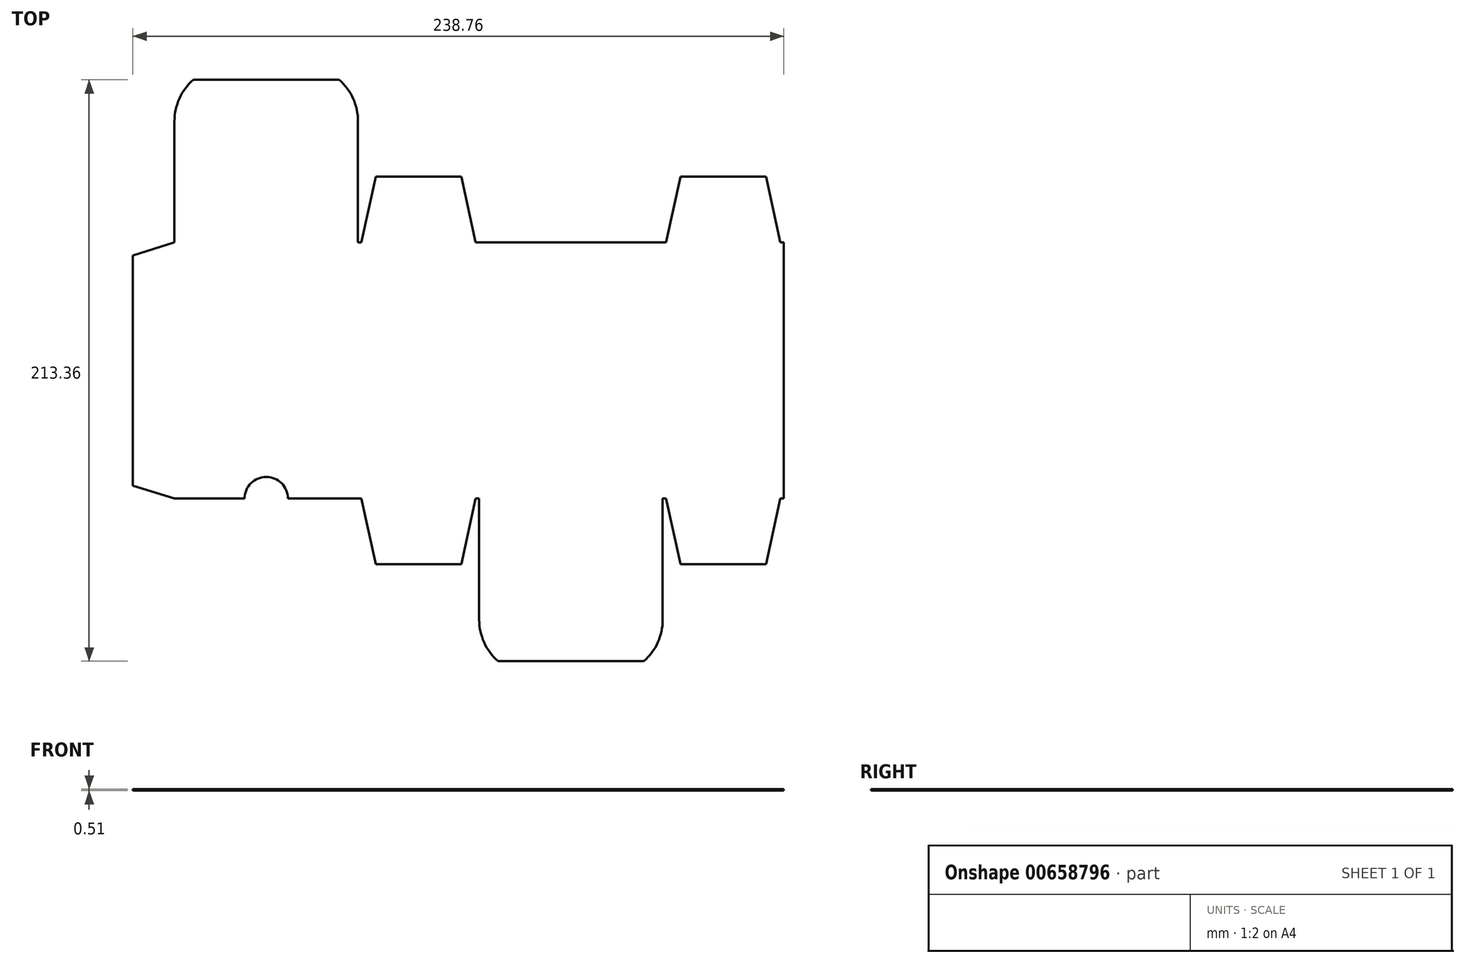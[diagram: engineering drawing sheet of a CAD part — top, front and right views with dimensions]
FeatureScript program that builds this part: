
annotation { "Feature Type Name" : "Feature", "Feature Type Description" : "" }
export const myFeature = defineFeature(function(context is Context, id is Id, definition is map)
    precondition{}
    {
        {
            var Q0;
            Q0=qCreatedBy(makeId("Top.planeOp"),FACE);
            var sketch = newSketch(context, id + "F0", { "sketchPlane" : qUnion([Q0])});
            skLineSegment(sketch, "E0.bottom", {"start": v(0, 0) * mm, "end": v(25.72, 0) * mm});
            skLineSegment(sketch, "E0.top", {"start": v(0, 93.98) * mm, "end": v(67.3, 93.98) * mm, "construction": true});
            skLineSegment(sketch, "E0.left", {"start": v(0, 0) * mm, "end": v(0, 93.98) * mm, "construction": true});
            skLineSegment(sketch, "E0.right", {"start": v(67.31, 0) * mm, "end": v(67.31, 93.98) * mm, "construction": true});
            skLineSegment(sketch, "E1", {"start": v(0, 93.98) * mm, "end": v(0, 138.43) * mm});
            skLineSegment(sketch, "E2", {"start": v(0, 138.43) * mm, "end": v(67.3, 138.43) * mm, "construction": true});
            skLineSegment(sketch, "E3", {"start": v(67.3, 138.43) * mm, "end": v(67.3, 93.98) * mm});
            skLineSegment(sketch, "E4", {"start": v(67.31, 0) * mm, "end": v(68.58, 0) * mm, "construction": true});
            skLineSegment(sketch, "E5", {"start": v(111.76, 93.98) * mm, "end": v(111.76, 0) * mm, "construction": true});
            skLineSegment(sketch, "E6", {"start": v(111.76, 0) * mm, "end": v(179.07, 0) * mm, "construction": true});
            skLineSegment(sketch, "E7", {"start": v(179.07, 0) * mm, "end": v(179.07, 93.98) * mm, "construction": true});
            skLineSegment(sketch, "E8", {"start": v(111.76, 93.98) * mm, "end": v(179.07, 93.98) * mm});
            skArc(sketch, "E9", {"start": v(6.88, 153.67) * mm, "mid": v(1.8, 146.8) * mm, "end": v(0, 138.43) * mm});
            skLineSegment(sketch, "E10", {"start": v(33.65, 93.98) * mm, "end": v(33.65, 138.43) * mm, "construction": true});
            skLineSegment(sketch, "E11", {"start": v(6.88, 153.67) * mm, "end": v(33.65, 153.67) * mm});
            skLineSegment(sketch, "E12.MirrorCS", {"start": v(60.43, 153.67) * mm, "end": v(33.65, 153.67) * mm});
            skArc(sketch, "E13.MirrorCS", {"start": v(60.43, 153.67) * mm, "mid": v(65.51, 146.8) * mm, "end": v(67.3, 138.43) * mm});
            skLineSegment(sketch, "E14", {"start": v(0, 47) * mm, "end": v(67.31, 47) * mm, "construction": true});
            skLineSegment(sketch, "E15", {"start": v(0, 93.98) * mm, "end": v(-15.24, 89.22) * mm});
            skLineSegment(sketch, "E16", {"start": v(-15.24, 89.22) * mm, "end": v(-15.24, 46.99) * mm});
            skLineSegment(sketch, "E17.MirrorCS", {"start": v(0, 0) * mm, "end": v(-15.24, 4.76) * mm});
            skLineSegment(sketch, "E18.MirrorCS", {"start": v(-15.24, 4.76) * mm, "end": v(-15.24, 46.99) * mm});
            skArc(sketch, "E19", {"start": v(41.6, 0) * mm, "mid": v(33.66, 7.94) * mm, "end": v(25.72, 0) * mm});
            skLineSegment(sketch, "E20.trimOffspring", {"start": v(41.6, 0) * mm, "end": v(67.31, 0) * mm});
            skLineSegment(sketch, "E21", {"start": v(67.3, 93.98) * mm, "end": v(68.58, 93.98) * mm});
            skLineSegment(sketch, "E22", {"start": v(111.76, 93.98) * mm, "end": v(110.5, 93.98) * mm});
            skLineSegment(sketch, "E23", {"start": v(89.53, 93.98) * mm, "end": v(89.53, 118.11) * mm, "construction": true});
            skLineSegment(sketch, "E24", {"start": v(68.58, 93.98) * mm, "end": v(73.86, 118.11) * mm});
            skLineSegment(sketch, "E25.MirrorCS", {"start": v(110.5, 93.98) * mm, "end": v(105.21, 118.11) * mm});
            skLineSegment(sketch, "E26", {"start": v(73.86, 118.11) * mm, "end": v(105.21, 118.11) * mm});
            skLineSegment(sketch, "E27.MirrorCS", {"start": v(110.5, 0) * mm, "end": v(105.21, -24.13) * mm});
            skLineSegment(sketch, "E28.MirrorCS", {"start": v(68.58, 0) * mm, "end": v(73.86, -24.13) * mm});
            skLineSegment(sketch, "E29.MirrorCS", {"start": v(73.86, -24.13) * mm, "end": v(105.21, -24.13) * mm});
            skLineSegment(sketch, "E30", {"start": v(179.07, 93.98) * mm, "end": v(223.52, 93.98) * mm, "construction": true});
            skLineSegment(sketch, "E31", {"start": v(223.52, 0) * mm, "end": v(223.52, 93.98) * mm});
            skLineSegment(sketch, "E32", {"start": v(145.42, 93.98) * mm, "end": v(145.42, 0) * mm, "construction": true});
            skLineSegment(sketch, "E33.MirrorCS", {"start": v(180.34, 93.98) * mm, "end": v(185.62, 118.11) * mm});
            skLineSegment(sketch, "E34.MirrorCS", {"start": v(216.97, 118.11) * mm, "end": v(185.62, 118.11) * mm});
            skLineSegment(sketch, "E35.MirrorCS", {"start": v(222.25, 93.98) * mm, "end": v(216.97, 118.11) * mm});
            skLineSegment(sketch, "E36.MirrorCS", {"start": v(222.25, 0) * mm, "end": v(216.97, -24.13) * mm});
            skLineSegment(sketch, "E37.MirrorCS", {"start": v(216.97, -24.13) * mm, "end": v(185.62, -24.13) * mm});
            skLineSegment(sketch, "E38.MirrorCS", {"start": v(180.34, 0) * mm, "end": v(185.62, -24.13) * mm});
            skLineSegment(sketch, "E39", {"start": v(68.58, 93.98) * mm, "end": v(110.5, 93.98) * mm, "construction": true});
            skLineSegment(sketch, "E40.trimOffspring", {"start": v(110.5, 0) * mm, "end": v(111.76, 0) * mm, "construction": true});
            skLineSegment(sketch, "E41", {"start": v(67.31, 0) * mm, "end": v(68.58, 0) * mm});
            skLineSegment(sketch, "E42", {"start": v(111.76, 0) * mm, "end": v(110.5, 0) * mm});
            skLineSegment(sketch, "E43", {"start": v(68.58, 0) * mm, "end": v(110.5, 0) * mm, "construction": true});
            skLineSegment(sketch, "E44", {"start": v(179.07, 0) * mm, "end": v(180.34, 0) * mm});
            skLineSegment(sketch, "E45.trimOffspring", {"start": v(222.25, 0) * mm, "end": v(223.52, 0) * mm});
            skLineSegment(sketch, "E46", {"start": v(180.34, 0) * mm, "end": v(222.25, 0) * mm, "construction": true});
            skLineSegment(sketch, "E47", {"start": v(111.76, 0) * mm, "end": v(111.76, -44.45) * mm});
            skLineSegment(sketch, "E48", {"start": v(179.07, 0) * mm, "end": v(179.07, -44.45) * mm});
            skLineSegment(sketch, "E49", {"start": v(111.76, -44.45) * mm, "end": v(179.07, -44.45) * mm, "construction": true});
            skArc(sketch, "E50", {"start": v(172.2, -59.69) * mm, "mid": v(177.27, -52.81) * mm, "end": v(179.07, -44.45) * mm});
            skArc(sketch, "E51", {"start": v(111.76, -44.45) * mm, "mid": v(113.56, -52.81) * mm, "end": v(118.64, -59.7) * mm});
            skLineSegment(sketch, "E52", {"start": v(172.2, -59.7) * mm, "end": v(118.64, -59.7) * mm});
            skLineSegment(sketch, "E53", {"start": v(179.07, 93.98) * mm, "end": v(180.34, 93.98) * mm});
            skLineSegment(sketch, "E54", {"start": v(222.25, 93.98) * mm, "end": v(223.52, 93.98) * mm});
            skSolve(sketch);
        }
        {
            var Q0;
            Q0=makeQuery(id+"F0.imprint","IMPRINT",FACE,{"disambiguationData":[TD([[makeQuery(id+"F0.imprint","IMPRINT",EDGE,{"derivedFrom":sQuery(id+"F0.wireOp",EDGE,"E0.bottom")}),1.0]])]});
            extrude(context, id + "F1", {"entities" : qUnion([Q0]), "depth" : 0.5 * mm, "offsetDistance" : 25.4 * mm});
        }
    });
